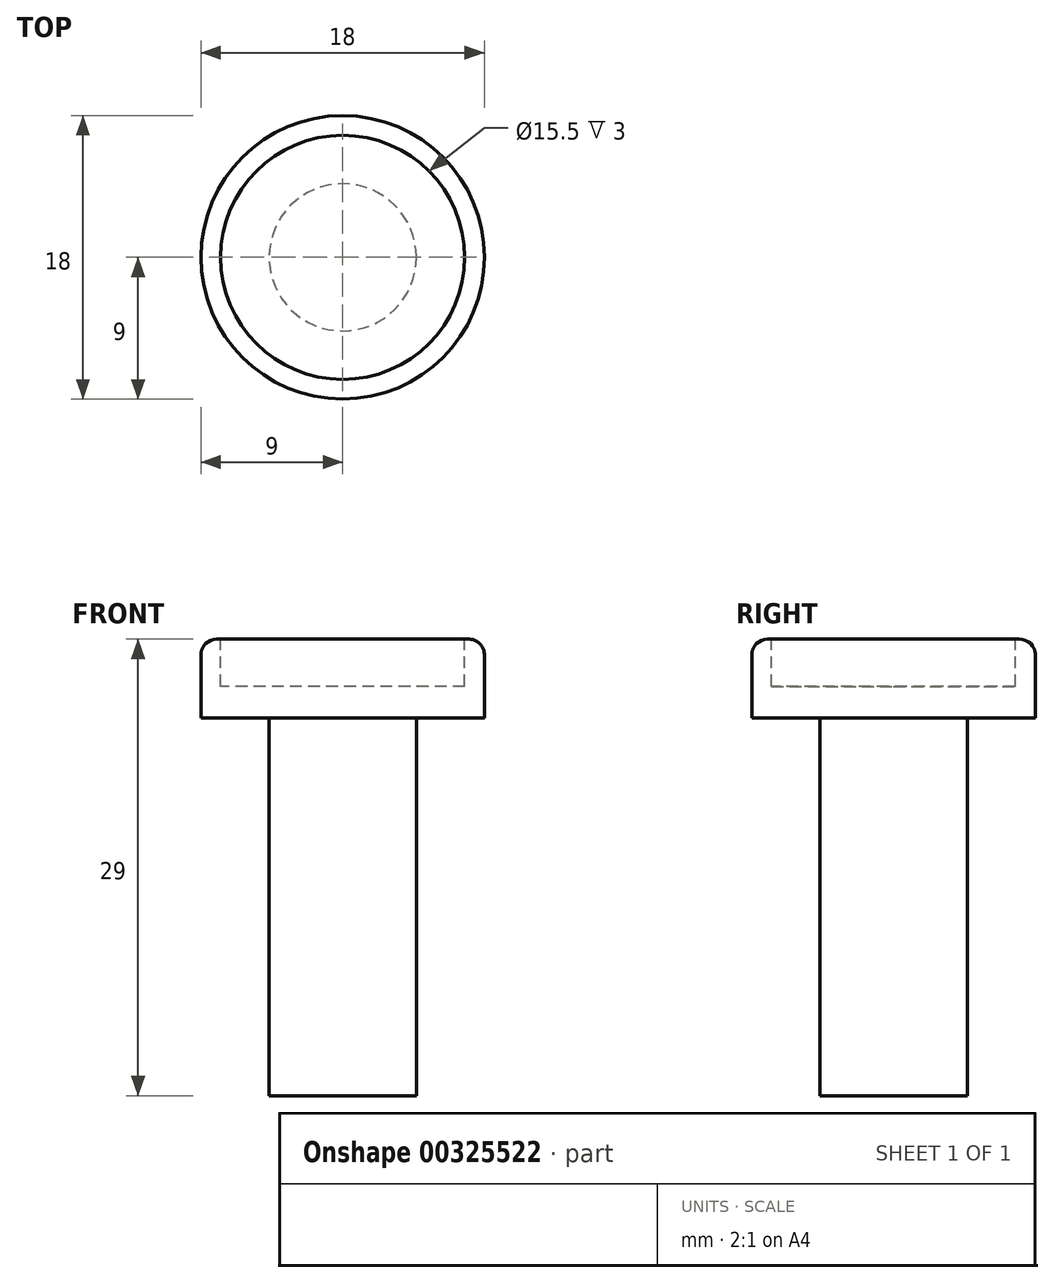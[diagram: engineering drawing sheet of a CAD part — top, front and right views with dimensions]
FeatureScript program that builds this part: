
annotation { "Feature Type Name" : "Feature", "Feature Type Description" : "" }
export const myFeature = defineFeature(function(context is Context, id is Id, definition is map)
    precondition{}
    {
        {
            var Q0;
            Q0=qCreatedBy(makeId("Top.planeOp"),FACE);
            var sketch = newSketch(context, id + "F0", { "sketchPlane" : qUnion([Q0])});
            skCircle(sketch, "E0", {"center": v(0, 0) * mm, "radius": 4.68 * mm});
            skSolve(sketch);
        }
        {
            var Q0;
            Q0 = qSketchRegion(id + "F0", true);
            extrude(context, id + "F1", {"entities" : qUnion([Q0]), "depth" : 24 * mm});
        }
        {
            var Q0;
            Q0=makeQuery(id+"F1.opExtrude","CAP_FACE",FACE,{"disambiguationData":[OSD([sQuery(id+"F0.wireOp",EDGE,"E0")])],"isStart":false});
            var sketch = newSketch(context, id + "F2", { "sketchPlane" : qUnion([Q0])});
            skCircle(sketch, "E1", {"center": v(0, 0) * mm, "radius": 9 * mm});
            skSolve(sketch);
        }
        {
            var Q0;
            Q0 = qSketchRegion(id + "F2", true);
            extrude(context, id + "F3", {"entities" : qUnion([Q0]), "operationType" : NewBodyOperationType.ADD, "depth" : 5 * mm});
        }
        {
            var Q0;
            Q0=makeQuery(id+"F3.opExtrude","CAP_FACE",FACE,{"disambiguationData":[OSD([sQuery(id+"F2.wireOp",EDGE,"E1")])],"isStart":false});
            var sketch = newSketch(context, id + "F4", { "sketchPlane" : qUnion([Q0])});
            skCircle(sketch, "E2", {"center": v(0, 0) * mm, "radius": 7.75 * mm});
            skSolve(sketch);
        }
        {
            var Q0;
            Q0 = qSketchRegion(id + "F4", true);
            extrude(context, id + "F5", {"entities" : qUnion([Q0]), "operationType" : NewBodyOperationType.REMOVE, "oppositeDirection" : true, "depth" : 3 * mm});
        }
        {
            var Q0;
            Q0=makeQuery(id+"F3.opExtrude","CAP_EDGE",EDGE,{"disambiguationData":[OSD([sQuery(id+"F2.wireOp",EDGE,"E1")])],"isStart":false});
            fillet(context, id + "F6", {"entities" : qUnion([Q0]), "radius" : 1 * mm, "tangentPropagation" : true, "allowEdgeOverflow" : false});
        }
    });
